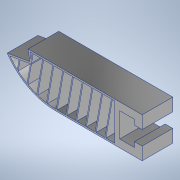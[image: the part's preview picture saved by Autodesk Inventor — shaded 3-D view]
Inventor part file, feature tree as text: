
AUTODESK INVENTOR PART (.ipt)
format: ipt  version: 2022 (Build 260153000, 153)  size: 292,352 bytes
history: native  units: mm
features: extrude x5, sketch x4, fillet x1, shell x1, projected_geometry x1
ambient origin geometry x8: Origin, YZ Plane, XZ Plane, XY Plane, X Axis, Y Axis, Z Axis, Center Point
bodies: Body1 (feature_tree)
feature tree (12):
  extrude  "Extrusion2"  Depth=5.8mm
  extrude  "Extrusion5"  Depth=12.0mm TaperAngle=0.0deg
  fillet  "Fillet2"  Radius=45.0mm
  shell  "Shell1"  Thickness=15.6mm
  extrude  "Extrusion7"  TaperAngle=0.0deg  [1 undecoded]
  extrude  "Extrusion8"  Depth=9.6mm
  extrude  "Extrusion9"  Depth=0.38mm
  sketch  "Sketch8"  dims[d41=5.8mm d48=44.0mm]
  sketch  "Sketch13"  dims[d50=3.0mm d56=12.0mm d57=0.0mm d63=45.0mm d67=15.6mm d71=0.0mm]
  sketch  "Sketch14"  dims[d80=17.453293mm d82=0.0mm d83=0.0mm]
  projected_geometry  "Projected Loop1"
  sketch  "Sketch15"  dims[d87=5.6mm d88=9.6mm d95=4.0mm d96=9.0mm d97=15.6mm d98=23.0mm d99=0.62mm d100=12.0mm d101=0.0mm d102=10.747401mm d103=12.0mm d104=0.0mm d105=0.38mm d1=0.38mm d127=12.0mm d128=0.0mm d129=3.81mm d130=17.453293mm d132=17.453293mm d133=0.38mm d135=0.38mm d136=0.38mm d137=0.38mm d138=0.38mm d139=0.38mm d140=0.38mm d141=0.38mm d142=3.81mm d143=0.38mm d144=3.81mm d145=3.81mm d146=3.81mm d147=3.81mm d148=3.81mm d149=3.81mm d150=3.81mm d151=3.81mm d152=17.453293mm]
note: 1 required parameter value undecoded (feature->parameter linkage not recoverable at this tier; creation-order binding heuristic only, values carry confidence <= 0.55)
